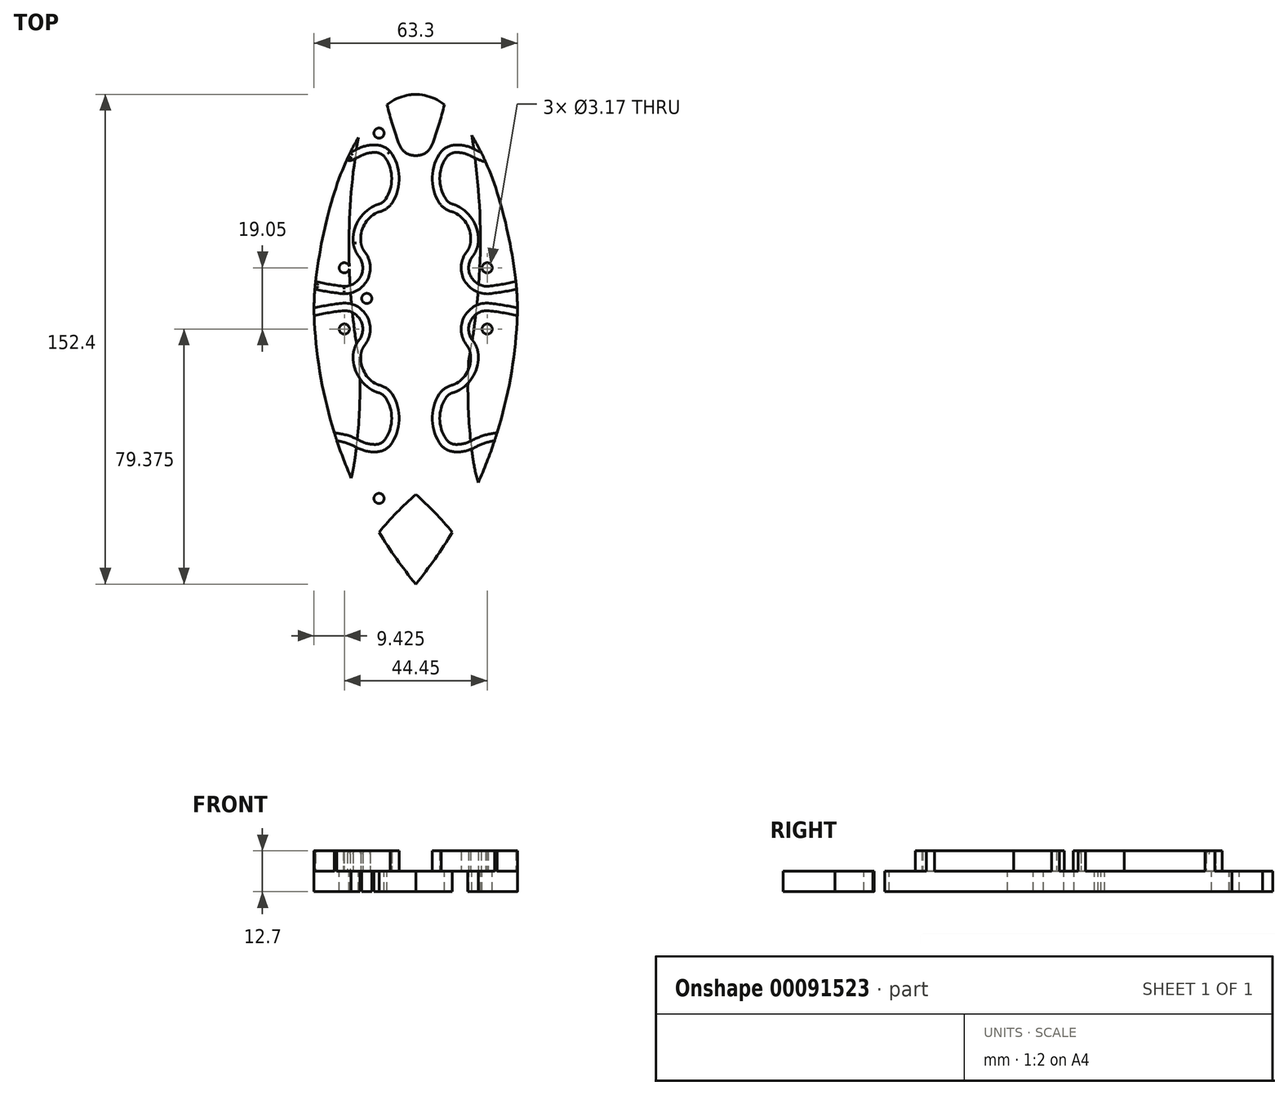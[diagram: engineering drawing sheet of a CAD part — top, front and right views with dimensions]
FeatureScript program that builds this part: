
annotation { "Feature Type Name" : "Feature", "Feature Type Description" : "" }
export const myFeature = defineFeature(function(context is Context, id is Id, definition is map)
    precondition{}
    {
        {
            var Q0;
            Q0=qCreatedBy(makeId("Top.planeOp"),FACE);
            var sketch = newSketch(context, id + "F0", { "sketchPlane" : qUnion([Q0])});
            skLineSegment(sketch, "E0", {"start": v(0, 0) * mm, "end": v(0, 80.69) * mm, "construction": true});
            skLineSegment(sketch, "E1", {"start": v(-64.8, 0) * mm, "end": v(76.72, 0) * mm, "construction": true});
            skLineSegment(sketch, "E2", {"start": v(0, 0) * mm, "end": v(0, -115.81) * mm, "construction": true});
            skPoint(sketch, "E3", {"position": v(0, 63.5) * mm});
            skPoint(sketch, "E4", {"position": v(31.75, 0) * mm});
            skPoint(sketch, "E5", {"position": v(-31.75, 0) * mm});
            skPoint(sketch, "E6", {"position": v(0, -88.9) * mm});
            skPoint(sketch, "E7", {"position": v(0, -19.05) * mm});
            skEllipticalArc(sketch, "E8", {});
            skPoint(sketch, "E9", {"position": v(0, -63.5) * mm});
            skPoint(sketch, "E10", {"position": v(16.51, -63.5) * mm});
            skArc(sketch, "E11", {"start": v(0, -88.9) * mm, "mid": v(22.23, -50.65) * mm, "end": v(31.54, -7.4) * mm});
            skArc(sketch, "E12.MirrorCS", {"start": v(0, -88.9) * mm, "mid": v(-22.23, -50.65) * mm, "end": v(-31.54, -7.4) * mm});
            skArc(sketch, "E13.filletArc", {"start": v(-31.03, 6.47) * mm, "mid": v(-31.6, -0.45) * mm, "end": v(-31.54, -7.4) * mm});
            skArc(sketch, "E14.MirrorCS", {"start": v(31.03, 6.47) * mm, "mid": v(31.6, -0.45) * mm, "end": v(31.54, -7.4) * mm});
            skPoint(sketch, "E15", {"position": v(-19.05, 76.2) * mm});
            skPoint(sketch, "E16", {"position": v(19.05, 76.2) * mm});
            skArc(sketch, "E17", {"start": v(-19.05, 47.97) * mm, "mid": v(-17.86, 62.09) * mm, "end": v(-19.05, 76.2) * mm});
            skArc(sketch, "E18", {"start": v(-19.05, 76.2) * mm, "mid": v(-11.04, 67.58) * mm, "end": v(0, 63.5) * mm});
            skArc(sketch, "E19.MirrorCS", {"start": v(19.05, 47.97) * mm, "mid": v(17.86, 62.09) * mm, "end": v(19.05, 76.2) * mm});
            skArc(sketch, "E20.MirrorCS", {"start": v(19.05, 76.2) * mm, "mid": v(11.04, 67.58) * mm, "end": v(0, 63.5) * mm});
            const initialGuessF0  = {"E8": [0, -0.01905, 0, 1, 0.08255, 0.03263075260586246, 5.026736623577707, 1.2564486836018787]};
            skSetInitialGuess(sketch, initialGuessF0);
            skSolve(sketch);
        }
        {
            var Q0;
            Q0=makeQuery(id+"F0.imprint","IMPRINT",FACE,{"disambiguationData":[TD([[makeQuery(id+"F0.imprint","IMPRINT",EDGE,{"derivedFrom":sQuery(id+"F0.wireOp",EDGE,"E8")}),1.0]])]});
            extrude(context, id + "F1", {"entities" : qUnion([Q0]), "oppositeDirection" : true, "depth" : 6.35 * mm});
        }
        {
            var Q0;
            Q0=qCreatedBy(makeId("Top.planeOp"),FACE);
            var sketch = newSketch(context, id + "F2", { "sketchPlane" : qUnion([Q0])});
            skLineSegment(sketch, "E21", {"start": v(0, -123.95) * mm, "end": v(0, 157.96) * mm, "construction": true});
            skLineSegment(sketch, "E22", {"start": v(104.8, 0) * mm, "end": v(-112.4, 0) * mm, "construction": true});
            skPoint(sketch, "E23", {"position": v(22.23, 0) * mm});
            skPoint(sketch, "E24", {"position": v(22.23, 9.52) * mm});
            skPoint(sketch, "E25", {"position": v(12.7, 0) * mm});
            skPoint(sketch, "E26", {"position": v(12.7, 41.27) * mm});
            skPoint(sketch, "E27", {"position": v(12.7, 33.34) * mm});
            skPoint(sketch, "E28", {"position": v(22.23, -15.88) * mm});
            skPoint(sketch, "E29", {"position": v(19.05, 0) * mm});
            skPoint(sketch, "E30", {"position": v(19.05, -31.46) * mm});
            skPoint(sketch, "E31", {"position": v(19.05, -39.84) * mm});
            skSolve(sketch);
        }
        {
            var Q0;
            Q0=qCreatedBy(makeId("Top.planeOp"),FACE);
            var sketch = newSketch(context, id + "F3", { "sketchPlane" : qUnion([Q0])});
            skPoint(sketch, "E32", {"position": v(76.2, 76.2) * mm});
            skLineSegment(sketch, "E33", {"start": v(-207.32, 0) * mm, "end": v(117.03, 0) * mm, "construction": true});
            skLineSegment(sketch, "E34", {"start": v(0, 0) * mm, "end": v(0, 84.75) * mm, "construction": true});
            skPoint(sketch, "E35", {"position": v(22.22, 9.52) * mm});
            skPoint(sketch, "E36", {"position": v(12.7, 33.34) * mm});
            skPoint(sketch, "E37", {"position": v(12.7, 41.28) * mm});
            skCircle(sketch, "E38", {"center": v(76.2, 76.2) * mm, "radius": 11.11 * mm});
            skArc(sketch, "E39", {"start": v(64.87, 81.94) * mm, "mid": v(76.2, 63.5) * mm, "end": v(87.53, 81.94) * mm});
            skCircle(sketch, "E40", {"center": v(76.2, 76.2) * mm, "radius": 15.88 * mm, "construction": true});
            skArc(sketch, "E41", {"start": v(21.55, 15.04) * mm, "mid": v(16.68, 9.19) * mm, "end": v(22.22, 3.97) * mm});
            skPoint(sketch, "E42", {"position": v(12.7, 27.37) * mm});
            skPoint(sketch, "E43", {"position": v(63.5, 76.2) * mm});
            skPoint(sketch, "E44", {"position": v(88.9, 76.2) * mm});
            skPoint(sketch, "E45", {"position": v(61.91, 63.5) * mm});
            skPoint(sketch, "E46", {"position": v(50.8, 46.04) * mm});
            skPoint(sketch, "E47", {"position": v(31.75, 41.28) * mm});
            skPoint(sketch, "E48", {"position": v(19.05, 42.86) * mm});
            skArc(sketch, "E49", {"start": v(50.8, 46.04) * mm, "mid": v(60.54, 59.7) * mm, "end": v(63.5, 76.2) * mm});
            skArc(sketch, "E50", {"start": v(23.54, 41.87) * mm, "mid": v(37.5, 41.77) * mm, "end": v(50.8, 46.04) * mm});
            skPoint(sketch, "E51", {"position": v(76.2, 127) * mm});
            skLineSegment(sketch, "E52", {"start": v(76.2, 76.2) * mm, "end": v(76.2, 127) * mm, "construction": true});
            skArc(sketch, "E53", {"start": v(77.79, 125.41) * mm, "mid": v(76.2, 127) * mm, "end": v(74.61, 125.41) * mm});
            skPoint(sketch, "E54", {"position": v(77.79, 125.41) * mm});
            skPoint(sketch, "E55", {"position": v(74.61, 125.41) * mm});
            skPoint(sketch, "E56", {"position": v(65.2, 82.55) * mm});
            skLineSegment(sketch, "E57", {"start": v(63.5, 76.2) * mm, "end": v(88.9, 76.2) * mm, "construction": true});
            skPoint(sketch, "E58", {"position": v(87.2, 82.55) * mm});
            skArc(sketch, "E59", {"start": v(77.79, 125.41) * mm, "mid": v(80.38, 104.21) * mm, "end": v(86.68, 83.8) * mm});
            skArc(sketch, "E60", {"start": v(65.72, 83.8) * mm, "mid": v(72.02, 104.21) * mm, "end": v(74.61, 125.41) * mm});
            skArc(sketch, "E61.filletArc", {"start": v(64.87, 81.94) * mm, "mid": v(65.31, 82.86) * mm, "end": v(65.72, 83.8) * mm});
            skArc(sketch, "E62.filletArc", {"start": v(86.68, 83.8) * mm, "mid": v(87.09, 82.86) * mm, "end": v(87.53, 81.94) * mm});
            skArc(sketch, "E63", {"start": v(87.53, 81.94) * mm, "mid": v(76.2, 88.9) * mm, "end": v(64.87, 81.94) * mm});
            skArc(sketch, "E64.0", {"start": v(80.56, 91.46) * mm, "mid": v(76.36, 92.07) * mm, "end": v(72.16, 91.55) * mm});
            skArc(sketch, "E65", {"start": v(76.52, 107.95) * mm, "mid": v(76.2, 108.27) * mm, "end": v(75.88, 107.95) * mm});
            skPoint(sketch, "E66", {"position": v(75.88, 107.95) * mm});
            skPoint(sketch, "E67", {"position": v(76.52, 107.95) * mm});
            skArc(sketch, "E68", {"start": v(72.16, 91.55) * mm, "mid": v(74.3, 99.69) * mm, "end": v(75.88, 107.95) * mm});
            skArc(sketch, "E69", {"start": v(76.52, 107.95) * mm, "mid": v(78.26, 99.64) * mm, "end": v(80.56, 91.46) * mm});
            skPoint(sketch, "E70", {"position": v(22.22, 3.97) * mm});
            skPoint(sketch, "E71", {"position": v(16.67, 9.52) * mm});
            skPoint(sketch, "E72", {"position": v(22.22, 15.08) * mm});
            skPoint(sketch, "E73", {"position": v(57.54, 53.98) * mm});
            skCircle(sketch, "E74", {"center": v(67.48, 46.06) * mm, "radius": 12.7 * mm, "construction": true});
            skLineSegment(sketch, "E75.bottom", {"start": v(57.54, 53.98) * mm, "end": v(77.4, 53.98) * mm, "construction": true});
            skLineSegment(sketch, "E75.top", {"start": v(57.54, 38.15) * mm, "end": v(77.4, 38.15) * mm, "construction": true});
            skLineSegment(sketch, "E75.left", {"start": v(57.54, 53.98) * mm, "end": v(57.54, 38.15) * mm, "construction": true});
            skLineSegment(sketch, "E75.right", {"start": v(77.4, 53.97) * mm, "end": v(77.4, 38.15) * mm, "construction": true});
            skArc(sketch, "E76", {"start": v(22.22, 3.97) * mm, "mid": v(69.22, 27.48) * mm, "end": v(88.9, 76.2) * mm});
            skCircle(sketch, "E77", {"center": v(12.7, 33.34) * mm, "radius": 3.97 * mm, "construction": true});
            skPoint(sketch, "E78", {"position": v(12.7, 45.24) * mm});
            skPoint(sketch, "E79", {"position": v(8.73, 41.28) * mm});
            skLineSegment(sketch, "E80.bottom", {"start": v(8.73, 41.28) * mm, "end": v(12.7, 41.28) * mm, "construction": true});
            skLineSegment(sketch, "E80.top", {"start": v(8.73, 45.24) * mm, "end": v(12.7, 45.24) * mm, "construction": true});
            skLineSegment(sketch, "E80.left", {"start": v(8.73, 41.28) * mm, "end": v(8.73, 45.24) * mm, "construction": true});
            skLineSegment(sketch, "E80.right", {"start": v(12.7, 41.28) * mm, "end": v(12.7, 45.24) * mm, "construction": true});
            skLineSegment(sketch, "E81", {"start": v(12.7, 41.27) * mm, "end": v(8.73, 45.24) * mm, "construction": true});
            skPoint(sketch, "E82", {"position": v(9.9, 44.08) * mm});
            skPoint(sketch, "E83", {"position": v(12.7, 37.3) * mm});
            skLineSegment(sketch, "E84", {"start": v(12.7, 37.3) * mm, "end": v(0, 37.3) * mm, "construction": true});
            skPoint(sketch, "E85.MirrorP", {"position": v(9.9, 30.53) * mm});
            skArc(sketch, "E86", {"start": v(9.9, 44.08) * mm, "mid": v(7.67, 37.3) * mm, "end": v(9.9, 30.53) * mm});
            skArc(sketch, "E87", {"start": v(12.7, 45.24) * mm, "mid": v(11.18, 44.94) * mm, "end": v(9.9, 44.08) * mm});
            skArc(sketch, "E88.MirrorCS", {"start": v(12.09, 29.42) * mm, "mid": v(10.9, 29.8) * mm, "end": v(9.9, 30.53) * mm});
            skArc(sketch, "E89", {"start": v(17.4, 44.02) * mm, "mid": v(15.13, 44.93) * mm, "end": v(12.7, 45.24) * mm});
            skArc(sketch, "E90.filletArc", {"start": v(17.4, 44.02) * mm, "mid": v(20.38, 42.68) * mm, "end": v(23.54, 41.87) * mm});
            skLineSegment(sketch, "E91", {"start": v(12.7, 37.3) * mm, "end": v(22.22, 9.52) * mm, "construction": true});
            skPoint(sketch, "E92", {"position": v(17.46, 23.42) * mm});
            skArc(sketch, "E93", {"start": v(17.46, 23.42) * mm, "mid": v(59, 36.27) * mm, "end": v(76.2, 76.2) * mm, "construction": true});
            skPoint(sketch, "E94", {"position": v(46.35, 27.89) * mm});
            skArc(sketch, "E95", {"start": v(23.97, 15.5) * mm, "mid": v(35.96, 20.26) * mm, "end": v(46.35, 27.89) * mm});
            skArc(sketch, "E96", {"start": v(13.98, 29.02) * mm, "mid": v(30.1, 26.65) * mm, "end": v(46.35, 27.89) * mm});
            skPoint(sketch, "E97.visualSharp", {"position": v(12.7, 29.37) * mm});
            skArc(sketch, "E97.filletArc", {"start": v(13.98, 29.02) * mm, "mid": v(13.04, 29.24) * mm, "end": v(12.09, 29.42) * mm});
            skArc(sketch, "E98.filletArc", {"start": v(21.55, 15.04) * mm, "mid": v(22.77, 15.23) * mm, "end": v(23.97, 15.5) * mm});
            skPoint(sketch, "E99", {"position": v(76.2, 92.08) * mm});
            skArc(sketch, "E100.MirrorCS", {"start": v(22.22, -3.97) * mm, "mid": v(69.22, -27.48) * mm, "end": v(88.9, -76.2) * mm});
            skArc(sketch, "E101.MirrorCS", {"start": v(21.55, -15.04) * mm, "mid": v(16.68, -9.19) * mm, "end": v(22.22, -3.97) * mm});
            skArc(sketch, "E102.MirrorCS", {"start": v(23.97, -15.5) * mm, "mid": v(35.96, -20.26) * mm, "end": v(46.35, -27.89) * mm});
            skArc(sketch, "E103.MirrorCS", {"start": v(13.98, -29.02) * mm, "mid": v(30.1, -26.65) * mm, "end": v(46.35, -27.89) * mm});
            skCircle(sketch, "E104.MirrorC", {"center": v(76.2, -76.2) * mm, "radius": 11.11 * mm});
            skArc(sketch, "E105.MirrorCS", {"start": v(64.87, -81.94) * mm, "mid": v(76.2, -63.5) * mm, "end": v(87.53, -81.94) * mm});
            skArc(sketch, "E106.MirrorCS", {"start": v(23.54, -41.87) * mm, "mid": v(37.5, -41.77) * mm, "end": v(50.8, -46.04) * mm});
            skArc(sketch, "E107.MirrorCS", {"start": v(77.79, -125.41) * mm, "mid": v(80.38, -104.21) * mm, "end": v(86.68, -83.8) * mm});
            skArc(sketch, "E108.MirrorCS", {"start": v(76.52, -107.95) * mm, "mid": v(78.26, -99.64) * mm, "end": v(80.56, -91.46) * mm});
            skArc(sketch, "E109.MirrorCS", {"start": v(72.16, -91.55) * mm, "mid": v(74.3, -99.69) * mm, "end": v(75.88, -107.95) * mm});
            skArc(sketch, "E110.MirrorCS", {"start": v(65.72, -83.8) * mm, "mid": v(72.02, -104.21) * mm, "end": v(74.61, -125.41) * mm});
            skArc(sketch, "E111.MirrorCS", {"start": v(80.56, -91.46) * mm, "mid": v(76.36, -92.07) * mm, "end": v(72.16, -91.55) * mm});
            skCircle(sketch, "E112.MirrorC", {"center": v(67.48, -46.06) * mm, "radius": 12.7 * mm, "construction": true});
            skArc(sketch, "E113.MirrorCS", {"start": v(50.8, -46.04) * mm, "mid": v(60.54, -59.7) * mm, "end": v(63.5, -76.2) * mm});
            skCircle(sketch, "E114.MirrorC", {"center": v(12.7, -33.34) * mm, "radius": 3.97 * mm, "construction": true});
            skCircle(sketch, "E115.MirrorC", {"center": v(12.7, -41.28) * mm, "radius": 3.97 * mm, "construction": true});
            skArc(sketch, "E116.MirrorCS", {"start": v(9.9, -44.08) * mm, "mid": v(7.67, -37.3) * mm, "end": v(9.9, -30.53) * mm});
            skArc(sketch, "E117.MirrorCS", {"start": v(13.98, -29.02) * mm, "mid": v(13.04, -29.24) * mm, "end": v(12.09, -29.42) * mm});
            skArc(sketch, "E118.MirrorCS", {"start": v(12.09, -29.42) * mm, "mid": v(10.9, -29.8) * mm, "end": v(9.9, -30.53) * mm});
            skArc(sketch, "E119.MirrorCS", {"start": v(17.4, -44.02) * mm, "mid": v(20.38, -42.68) * mm, "end": v(23.54, -41.87) * mm});
            skArc(sketch, "E120.MirrorCS", {"start": v(17.4, -44.02) * mm, "mid": v(15.13, -44.93) * mm, "end": v(12.7, -45.24) * mm});
            skArc(sketch, "E121.MirrorCS", {"start": v(21.55, -15.04) * mm, "mid": v(22.77, -15.23) * mm, "end": v(23.97, -15.5) * mm});
            skArc(sketch, "E122.0", {"start": v(13.33, 26.56) * mm, "mid": v(30.01, 24.11) * mm, "end": v(46.83, 25.4) * mm});
            skArc(sketch, "E122.1", {"start": v(13.33, 26.56) * mm, "mid": v(12.52, 26.76) * mm, "end": v(11.7, 26.9) * mm});
            skArc(sketch, "E122.2", {"start": v(18.64, 46.24) * mm, "mid": v(15.77, 47.4) * mm, "end": v(12.7, 47.78) * mm});
            skArc(sketch, "E122.3", {"start": v(12.7, 47.78) * mm, "mid": v(10.11, 47.25) * mm, "end": v(7.95, 45.73) * mm});
            skArc(sketch, "E122.4", {"start": v(7.95, 45.73) * mm, "mid": v(5.13, 37.3) * mm, "end": v(7.95, 28.88) * mm});
            skArc(sketch, "E122.5", {"start": v(11.7, 26.9) * mm, "mid": v(9.66, 27.58) * mm, "end": v(7.95, 28.88) * mm});
            skArc(sketch, "E123.0", {"start": v(18.64, 46.24) * mm, "mid": v(21.22, 45.08) * mm, "end": v(23.96, 44.37) * mm});
            skSolve(sketch);
        }
        {
            var Q0;
            Q0 = qSketchRegion(id + "F3", true);
            var sketch = newSketch(context, id + "F4", { "sketchPlane" : qUnion([Q0])});
            skFitSpline(sketch, "E124.0", {"points": [v(0, 63.5) * mm, v(-8.65, 63.5) * mm, v(-16.95, 54.8) * mm, v(-29.2, 23.84) * mm, v(-32.63, 2.84) * mm, v(-32.63, -40.94) * mm, v(-29.2, -61.94) * mm, v(-16.95, -92.9) * mm, v(-8.65, -101.6) * mm, v(8.65, -101.6) * mm, v(16.95, -92.9) * mm, v(29.2, -61.94) * mm, v(32.63, -40.94) * mm, v(32.63, 2.84) * mm, v(29.2, 23.84) * mm, v(16.95, 54.8) * mm, v(8.65, 63.5) * mm, v(0, 63.5) * mm]});
            skArc(sketch, "E125.0", {"start": v(23.34, 17.96) * mm, "mid": v(26.1, 18.75) * mm, "end": v(28.8, 19.71) * mm});
            skArc(sketch, "E125.1", {"start": v(21.24, 17.56) * mm, "mid": v(22.3, 17.73) * mm, "end": v(23.34, 17.96) * mm});
            skArc(sketch, "E125.2", {"start": v(21.24, 17.56) * mm, "mid": v(14.15, 8.96) * mm, "end": v(22.37, 1.43) * mm});
            skArc(sketch, "E125.3", {"start": v(22.37, 1.43) * mm, "mid": v(26.9, 2.03) * mm, "end": v(31.4, 2.9) * mm});
            skArc(sketch, "E126.0", {"start": v(22.23, 3.78) * mm, "mid": v(26.73, 4.38) * mm, "end": v(31.18, 5.25) * mm});
            skArc(sketch, "E126.1", {"start": v(21.53, 15.23) * mm, "mid": v(16.49, 9.17) * mm, "end": v(22.23, 3.78) * mm});
            skArc(sketch, "E126.2", {"start": v(21.53, 15.23) * mm, "mid": v(22.73, 15.42) * mm, "end": v(23.93, 15.68) * mm});
            skArc(sketch, "E126.3", {"start": v(23.93, 15.68) * mm, "mid": v(26.63, 16.45) * mm, "end": v(29.28, 17.38) * mm});
            skFitSpline(sketch, "E127.0", {"points": [v(0, 63.5) * mm, v(-8.65, 63.5) * mm, v(-16.95, 54.8) * mm, v(-29.2, 23.84) * mm, v(-32.63, 2.84) * mm, v(-32.63, -40.94) * mm, v(-29.2, -61.94) * mm, v(-16.95, -92.9) * mm, v(-8.65, -101.6) * mm, v(8.65, -101.6) * mm, v(16.95, -92.9) * mm, v(29.2, -61.94) * mm, v(32.63, -40.94) * mm, v(32.63, 2.84) * mm, v(29.2, 23.84) * mm, v(16.95, 54.8) * mm, v(8.65, 63.5) * mm, v(0, 63.5) * mm]});
            skFitSpline(sketch, "E128.0", {"points": [v(0, 63.5) * mm, v(-8.65, 63.5) * mm, v(-16.95, 54.8) * mm, v(-29.2, 23.84) * mm, v(-32.63, 2.84) * mm, v(-32.63, -40.94) * mm, v(-29.2, -61.94) * mm, v(-16.95, -92.9) * mm, v(-8.65, -101.6) * mm, v(8.65, -101.6) * mm, v(16.95, -92.9) * mm, v(29.2, -61.94) * mm, v(32.63, -40.94) * mm, v(32.63, 2.84) * mm, v(29.2, 23.84) * mm, v(16.95, 54.8) * mm, v(8.65, 63.5) * mm, v(0, 63.5) * mm]});
            skLineSegment(sketch, "E129", {"start": v(27.18, 26.62) * mm, "end": v(27.79, 24.22) * mm});
            skArc(sketch, "E130.MirrorCS", {"start": v(-21.24, 17.56) * mm, "mid": v(-14.15, 8.96) * mm, "end": v(-22.37, 1.43) * mm});
            skArc(sketch, "E131.MirrorCS", {"start": v(-21.24, 17.56) * mm, "mid": v(-22.3, 17.73) * mm, "end": v(-23.34, 17.96) * mm});
            skArc(sketch, "E132.MirrorCS", {"start": v(-23.34, 17.96) * mm, "mid": v(-26.1, 18.75) * mm, "end": v(-28.8, 19.71) * mm});
            skArc(sketch, "E133.MirrorCS", {"start": v(-23.93, 15.68) * mm, "mid": v(-26.63, 16.45) * mm, "end": v(-29.28, 17.38) * mm});
            skArc(sketch, "E134.MirrorCS", {"start": v(-21.53, 15.23) * mm, "mid": v(-22.73, 15.42) * mm, "end": v(-23.93, 15.68) * mm});
            skArc(sketch, "E135.MirrorCS", {"start": v(-21.53, 15.23) * mm, "mid": v(-16.49, 9.17) * mm, "end": v(-22.23, 3.78) * mm});
            skArc(sketch, "E136.MirrorCS", {"start": v(-22.23, 3.78) * mm, "mid": v(-26.73, 4.38) * mm, "end": v(-31.18, 5.25) * mm});
            skArc(sketch, "E137.MirrorCS", {"start": v(-22.37, 1.43) * mm, "mid": v(-26.9, 2.03) * mm, "end": v(-31.4, 2.9) * mm});
            skArc(sketch, "E138.MirrorCS", {"start": v(-31.18, 5.25) * mm, "mid": v(-31.3, 4.07) * mm, "end": v(-31.4, 2.9) * mm});
            skArc(sketch, "E139.MirrorCS", {"start": v(21.24, -17.56) * mm, "mid": v(14.15, -8.96) * mm, "end": v(22.37, -1.43) * mm});
            skArc(sketch, "E140.MirrorCS", {"start": v(21.53, -15.23) * mm, "mid": v(16.49, -9.17) * mm, "end": v(22.23, -3.78) * mm});
            skArc(sketch, "E141.MirrorCS", {"start": v(21.24, -17.56) * mm, "mid": v(22.3, -17.73) * mm, "end": v(23.34, -17.96) * mm});
            skArc(sketch, "E142.MirrorCS", {"start": v(21.53, -15.23) * mm, "mid": v(22.73, -15.42) * mm, "end": v(23.93, -15.68) * mm});
            skPoint(sketch, "E143.MirrorCS.end.orphan", {"position": v(-28.8, -19.71) * mm});
            skPoint(sketch, "E143.MirrorCS.start.orphan", {"position": v(-23.34, -17.96) * mm});
            skPoint(sketch, "E144.MirrorCS.end.orphan", {"position": v(-29.28, -17.38) * mm});
            skPoint(sketch, "E144.MirrorCS.start.orphan", {"position": v(-23.93, -15.68) * mm});
            skPoint(sketch, "E145.MirrorCS.end.orphan", {"position": v(-31.18, -5.25) * mm});
            skPoint(sketch, "E145.MirrorCS.start.orphan", {"position": v(-22.23, -3.78) * mm});
            skPoint(sketch, "E146.MirrorCS.end.orphan", {"position": v(-31.4, -2.9) * mm});
            skPoint(sketch, "E146.MirrorCS.start.orphan", {"position": v(-22.37, -1.43) * mm});
            skPoint(sketch, "E147.MirrorCS.end.orphan", {"position": v(31.4, -2.9) * mm});
            skPoint(sketch, "E147.MirrorCS.start.orphan", {"position": v(31.18, -5.25) * mm});
            skArc(sketch, "E148.0", {"start": v(31.18, 5.25) * mm, "mid": v(31.3, 4.07) * mm, "end": v(31.4, 2.9) * mm});
            skArc(sketch, "E148.1", {"start": v(30.24, -20.3) * mm, "mid": v(30.41, -19.1) * mm, "end": v(30.57, -17.89) * mm});
            skPoint(sketch, "E149.MirrorCS.start.orphan", {"position": v(22.23, -3.78) * mm});
            skPoint(sketch, "E150.MirrorCS.start.orphan", {"position": v(22.37, -1.43) * mm});
            skPoint(sketch, "E151.MirrorCS.end.orphan", {"position": v(29.28, -17.38) * mm});
            skPoint(sketch, "E151.MirrorCS.start.orphan", {"position": v(23.93, -15.68) * mm});
            skPoint(sketch, "E152.MirrorCS.end.orphan", {"position": v(28.8, -19.71) * mm});
            skPoint(sketch, "E152.MirrorCS.start.orphan", {"position": v(23.34, -17.96) * mm});
            skArc(sketch, "E153.0", {"start": v(22.48, -1.44) * mm, "mid": v(27.1, -2.06) * mm, "end": v(31.65, -2.95) * mm});
            skArc(sketch, "E154.0", {"start": v(22.24, -3.78) * mm, "mid": v(26.96, -4.42) * mm, "end": v(31.62, -5.35) * mm});
            skArc(sketch, "E155.0", {"start": v(23.34, -17.96) * mm, "mid": v(26.83, -19) * mm, "end": v(30.24, -20.3) * mm});
            skArc(sketch, "E156.0", {"start": v(23.93, -15.68) * mm, "mid": v(27.29, -16.67) * mm, "end": v(30.57, -17.89) * mm});
            skArc(sketch, "E157.trimOffspring", {"start": v(31.65, -2.95) * mm, "mid": v(31.65, -4.15) * mm, "end": v(31.62, -5.35) * mm});
            skArc(sketch, "E158", {"start": v(22.48, -1.44) * mm, "mid": v(22.43, -1.43) * mm, "end": v(22.37, -1.43) * mm});
            skArc(sketch, "E159", {"start": v(22.24, -3.78) * mm, "mid": v(22.24, -3.78) * mm, "end": v(22.23, -3.78) * mm});
            skArc(sketch, "E160", {"start": v(-28.8, 19.71) * mm, "mid": v(-29.07, 18.55) * mm, "end": v(-29.28, 17.38) * mm});
            skArc(sketch, "E161.MirrorCS", {"start": v(-31.65, -2.95) * mm, "mid": v(-31.65, -4.15) * mm, "end": v(-31.62, -5.35) * mm});
            skArc(sketch, "E162.MirrorCS", {"start": v(-22.48, -1.44) * mm, "mid": v(-27.1, -2.06) * mm, "end": v(-31.65, -2.95) * mm});
            skArc(sketch, "E163.MirrorCS", {"start": v(-22.24, -3.78) * mm, "mid": v(-26.96, -4.42) * mm, "end": v(-31.62, -5.35) * mm});
            skArc(sketch, "E164.MirrorCS", {"start": v(-21.53, -15.23) * mm, "mid": v(-16.49, -9.17) * mm, "end": v(-22.23, -3.78) * mm});
            skArc(sketch, "E165.MirrorCS", {"start": v(-21.24, -17.56) * mm, "mid": v(-14.15, -8.96) * mm, "end": v(-22.37, -1.43) * mm});
            skArc(sketch, "E166.MirrorCS", {"start": v(-22.48, -1.44) * mm, "mid": v(-22.43, -1.43) * mm, "end": v(-22.37, -1.43) * mm});
            skArc(sketch, "E167.MirrorCS", {"start": v(-22.24, -3.78) * mm, "mid": v(-22.24, -3.78) * mm, "end": v(-22.23, -3.78) * mm});
            skArc(sketch, "E168.MirrorCS", {"start": v(-21.53, -15.23) * mm, "mid": v(-22.73, -15.42) * mm, "end": v(-23.93, -15.68) * mm});
            skArc(sketch, "E169.MirrorCS", {"start": v(-21.24, -17.56) * mm, "mid": v(-22.3, -17.73) * mm, "end": v(-23.34, -17.96) * mm});
            skArc(sketch, "E170.MirrorCS", {"start": v(-23.34, -17.96) * mm, "mid": v(-26.83, -19) * mm, "end": v(-30.24, -20.3) * mm});
            skArc(sketch, "E171.MirrorCS", {"start": v(-23.93, -15.68) * mm, "mid": v(-27.29, -16.67) * mm, "end": v(-30.57, -17.89) * mm});
            skArc(sketch, "E172.MirrorCS", {"start": v(-30.24, -20.3) * mm, "mid": v(-30.41, -19.1) * mm, "end": v(-30.57, -17.89) * mm});
            skLineSegment(sketch, "E173", {"start": v(-51.74, 0) * mm, "end": v(55.96, 0) * mm, "construction": true});
            skLineSegment(sketch, "E174", {"start": v(0, 72.52) * mm, "end": v(0, -77) * mm, "construction": true});
            skSolve(sketch);
        }
        {
            var Q0;
            Q0=qCreatedBy(makeId("Top.planeOp"),FACE);
            var sketch = newSketch(context, id + "F5", { "sketchPlane" : qUnion([Q0])});
            skArc(sketch, "E175", {"start": v(21.77, 42.45) * mm, "mid": v(21.1, 43.93) * mm, "end": v(20.4, 45.4) * mm});
            skArc(sketch, "E176", {"start": v(27.79, 24.22) * mm, "mid": v(27.51, 25.43) * mm, "end": v(27.18, 26.62) * mm});
            skArc(sketch, "E177.0", {"start": v(17.5, 44.19) * mm, "mid": v(19.58, 43.19) * mm, "end": v(21.77, 42.45) * mm});
            skArc(sketch, "E177.1", {"start": v(13.93, 28.84) * mm, "mid": v(20.5, 27.43) * mm, "end": v(27.18, 26.62) * mm});
            skArc(sketch, "E177.2", {"start": v(13.93, 28.84) * mm, "mid": v(12.97, 29.06) * mm, "end": v(12, 29.24) * mm});
            skArc(sketch, "E177.3", {"start": v(9.42, 43.73) * mm, "mid": v(7.48, 37.32) * mm, "end": v(9.4, 30.9) * mm});
            skArc(sketch, "E177.4", {"start": v(17.5, 44.19) * mm, "mid": v(15.1, 45.14) * mm, "end": v(12.52, 45.43) * mm});
            skPoint(sketch, "E178.visualSharp", {"position": v(10.58, 29.4) * mm});
            skArc(sketch, "E178.filletArc", {"start": v(9.4, 30.9) * mm, "mid": v(10.53, 29.8) * mm, "end": v(12, 29.24) * mm});
            skPoint(sketch, "E179.visualSharp", {"position": v(10.57, 45.2) * mm});
            skArc(sketch, "E179.filletArc", {"start": v(12.52, 45.43) * mm, "mid": v(10.76, 44.96) * mm, "end": v(9.42, 43.73) * mm});
            skArc(sketch, "E180.0", {"start": v(18.64, 46.24) * mm, "mid": v(19.5, 45.8) * mm, "end": v(20.4, 45.4) * mm});
            skArc(sketch, "E180.1", {"start": v(18.64, 46.24) * mm, "mid": v(15.77, 47.4) * mm, "end": v(12.7, 47.78) * mm});
            skArc(sketch, "E180.2", {"start": v(12.7, 47.78) * mm, "mid": v(10.11, 47.25) * mm, "end": v(7.95, 45.73) * mm});
            skArc(sketch, "E180.3", {"start": v(13.33, 26.56) * mm, "mid": v(20.5, 25.05) * mm, "end": v(27.79, 24.22) * mm});
            skArc(sketch, "E180.4", {"start": v(13.33, 26.56) * mm, "mid": v(12.52, 26.76) * mm, "end": v(11.7, 26.9) * mm});
            skArc(sketch, "E180.5", {"start": v(11.7, 26.9) * mm, "mid": v(9.66, 27.58) * mm, "end": v(7.95, 28.88) * mm});
            skArc(sketch, "E180.6", {"start": v(7.95, 45.73) * mm, "mid": v(5.13, 37.3) * mm, "end": v(7.95, 28.88) * mm});
            skArc(sketch, "E181.MirrorCS", {"start": v(-7.95, 45.73) * mm, "mid": v(-5.13, 37.3) * mm, "end": v(-7.95, 28.88) * mm});
            skArc(sketch, "E182.MirrorCS", {"start": v(-12.7, 47.78) * mm, "mid": v(-10.11, 47.25) * mm, "end": v(-7.95, 45.73) * mm});
            skArc(sketch, "E183.MirrorCS", {"start": v(-18.64, 46.24) * mm, "mid": v(-15.77, 47.4) * mm, "end": v(-12.7, 47.78) * mm});
            skArc(sketch, "E184.MirrorCS", {"start": v(-12.52, 45.43) * mm, "mid": v(-10.76, 44.96) * mm, "end": v(-9.42, 43.73) * mm});
            skArc(sketch, "E185.MirrorCS", {"start": v(-9.42, 43.73) * mm, "mid": v(-7.48, 37.32) * mm, "end": v(-9.4, 30.9) * mm});
            skArc(sketch, "E186.MirrorCS", {"start": v(-9.4, 30.9) * mm, "mid": v(-10.53, 29.8) * mm, "end": v(-12, 29.24) * mm});
            skArc(sketch, "E187.MirrorCS", {"start": v(-11.7, 26.9) * mm, "mid": v(-9.66, 27.58) * mm, "end": v(-7.95, 28.88) * mm});
            skArc(sketch, "E188.MirrorCS", {"start": v(-13.33, 26.56) * mm, "mid": v(-12.52, 26.76) * mm, "end": v(-11.7, 26.9) * mm});
            skArc(sketch, "E189.MirrorCS", {"start": v(-13.93, 28.84) * mm, "mid": v(-12.97, 29.06) * mm, "end": v(-12, 29.24) * mm});
            skArc(sketch, "E190.MirrorCS", {"start": v(-13.93, 28.84) * mm, "mid": v(-20.5, 27.43) * mm, "end": v(-27.18, 26.62) * mm});
            skArc(sketch, "E191.MirrorCS", {"start": v(-13.33, 26.56) * mm, "mid": v(-20.5, 25.05) * mm, "end": v(-27.79, 24.22) * mm});
            skArc(sketch, "E192.MirrorCS", {"start": v(-17.5, 44.19) * mm, "mid": v(-19.58, 43.19) * mm, "end": v(-21.77, 42.45) * mm});
            skArc(sketch, "E193.MirrorCS", {"start": v(-17.5, 44.19) * mm, "mid": v(-15.1, 45.14) * mm, "end": v(-12.52, 45.43) * mm});
            skArc(sketch, "E194.MirrorCS", {"start": v(-18.64, 46.24) * mm, "mid": v(-19.5, 45.8) * mm, "end": v(-20.4, 45.4) * mm});
            skArc(sketch, "E195.MirrorCS", {"start": v(-21.77, 42.45) * mm, "mid": v(-21.1, 43.93) * mm, "end": v(-20.4, 45.4) * mm});
            skArc(sketch, "E196.MirrorCS", {"start": v(-27.79, 24.22) * mm, "mid": v(-27.51, 25.43) * mm, "end": v(-27.18, 26.62) * mm});
            skArc(sketch, "E197.MirrorCS", {"start": v(13.33, -26.56) * mm, "mid": v(12.52, -26.76) * mm, "end": v(11.7, -26.9) * mm});
            skArc(sketch, "E198.MirrorCS", {"start": v(11.7, -26.9) * mm, "mid": v(9.66, -27.58) * mm, "end": v(7.95, -28.88) * mm});
            skArc(sketch, "E199.MirrorCS", {"start": v(7.95, -45.73) * mm, "mid": v(5.13, -37.3) * mm, "end": v(7.95, -28.88) * mm});
            skArc(sketch, "E200.MirrorCS", {"start": v(12.7, -47.78) * mm, "mid": v(10.11, -47.25) * mm, "end": v(7.95, -45.73) * mm});
            skArc(sketch, "E201.MirrorCS", {"start": v(9.42, -43.73) * mm, "mid": v(7.48, -37.32) * mm, "end": v(9.4, -30.9) * mm});
            skArc(sketch, "E202.MirrorCS", {"start": v(9.4, -30.9) * mm, "mid": v(10.53, -29.8) * mm, "end": v(12, -29.24) * mm});
            skArc(sketch, "E203.MirrorCS", {"start": v(13.93, -28.84) * mm, "mid": v(12.97, -29.06) * mm, "end": v(12, -29.24) * mm});
            skArc(sketch, "E204.MirrorCS", {"start": v(17.5, -44.19) * mm, "mid": v(15.1, -45.14) * mm, "end": v(12.52, -45.43) * mm});
            skArc(sketch, "E205.MirrorCS", {"start": v(12.52, -45.43) * mm, "mid": v(10.76, -44.96) * mm, "end": v(9.42, -43.73) * mm});
            skArc(sketch, "E206.MirrorCS", {"start": v(18.64, -46.24) * mm, "mid": v(15.77, -47.4) * mm, "end": v(12.7, -47.78) * mm});
            skArc(sketch, "E207.0", {"start": v(24.52, -44.28) * mm, "mid": v(24.93, -43.04) * mm, "end": v(25.32, -41.8) * mm});
            skPoint(sketch, "E208.MirrorCS.end.orphan", {"position": v(27.18, -26.62) * mm});
            skPoint(sketch, "E208.MirrorCS.start.orphan", {"position": v(13.93, -28.84) * mm});
            skPoint(sketch, "E209.MirrorCS.end.orphan", {"position": v(27.79, -24.22) * mm});
            skPoint(sketch, "E209.MirrorCS.start.orphan", {"position": v(13.33, -26.56) * mm});
            skPoint(sketch, "E210.MirrorCS.end.orphan", {"position": v(21.77, -42.45) * mm});
            skPoint(sketch, "E210.MirrorCS.start.orphan", {"position": v(17.5, -44.19) * mm});
            skPoint(sketch, "E211.MirrorCS.end.orphan", {"position": v(20.4, -45.4) * mm});
            skPoint(sketch, "E211.MirrorCS.start.orphan", {"position": v(18.64, -46.24) * mm});
            skArc(sketch, "E212.0", {"start": v(13.33, -26.56) * mm, "mid": v(21.4, -24.9) * mm, "end": v(29.62, -24.13) * mm});
            skArc(sketch, "E213.0", {"start": v(13.93, -28.84) * mm, "mid": v(21.5, -27.27) * mm, "end": v(29.18, -26.5) * mm});
            skArc(sketch, "E214.0", {"start": v(23.96, -44.37) * mm, "mid": v(24.24, -44.33) * mm, "end": v(24.52, -44.28) * mm});
            skArc(sketch, "E214.1", {"start": v(18.64, -46.24) * mm, "mid": v(21.22, -45.08) * mm, "end": v(23.96, -44.37) * mm});
            skArc(sketch, "E215.0", {"start": v(23.57, -42.06) * mm, "mid": v(24.45, -41.92) * mm, "end": v(25.32, -41.8) * mm});
            skArc(sketch, "E215.1", {"start": v(17.5, -44.19) * mm, "mid": v(20.44, -42.86) * mm, "end": v(23.57, -42.06) * mm});
            skArc(sketch, "E216.trimOffspring", {"start": v(29.18, -26.5) * mm, "mid": v(29.4, -25.31) * mm, "end": v(29.62, -24.13) * mm});
            skArc(sketch, "E217.MirrorCS", {"start": v(-23.57, -42.06) * mm, "mid": v(-24.45, -41.92) * mm, "end": v(-25.32, -41.8) * mm});
            skArc(sketch, "E218.MirrorCS", {"start": v(-23.96, -44.37) * mm, "mid": v(-24.24, -44.33) * mm, "end": v(-24.52, -44.28) * mm});
            skArc(sketch, "E219.MirrorCS", {"start": v(-13.33, -26.56) * mm, "mid": v(-12.52, -26.76) * mm, "end": v(-11.7, -26.9) * mm});
            skPoint(sketch, "E220.MirrorP", {"position": v(-21.77, -42.45) * mm});
            skArc(sketch, "E221.MirrorCS", {"start": v(-13.93, -28.84) * mm, "mid": v(-12.97, -29.06) * mm, "end": v(-12, -29.24) * mm});
            skArc(sketch, "E222.MirrorCS", {"start": v(-17.5, -44.19) * mm, "mid": v(-20.44, -42.86) * mm, "end": v(-23.57, -42.06) * mm});
            skArc(sketch, "E223.MirrorCS", {"start": v(-18.64, -46.24) * mm, "mid": v(-15.77, -47.4) * mm, "end": v(-12.7, -47.78) * mm});
            skArc(sketch, "E224.MirrorCS", {"start": v(-11.7, -26.9) * mm, "mid": v(-9.66, -27.58) * mm, "end": v(-7.95, -28.88) * mm});
            skPoint(sketch, "E225.MirrorP", {"position": v(-17.5, -44.19) * mm});
            skArc(sketch, "E226.MirrorCS", {"start": v(-18.64, -46.24) * mm, "mid": v(-21.22, -45.08) * mm, "end": v(-23.96, -44.37) * mm});
            skPoint(sketch, "E227.MirrorP", {"position": v(-20.4, -45.4) * mm});
            skArc(sketch, "E228.MirrorCS", {"start": v(-7.95, -45.73) * mm, "mid": v(-5.13, -37.3) * mm, "end": v(-7.95, -28.88) * mm});
            skPoint(sketch, "E229.MirrorP", {"position": v(-27.79, -24.22) * mm});
            skArc(sketch, "E230.MirrorCS", {"start": v(-12.52, -45.43) * mm, "mid": v(-10.76, -44.96) * mm, "end": v(-9.42, -43.73) * mm});
            skArc(sketch, "E231.MirrorCS", {"start": v(-17.5, -44.19) * mm, "mid": v(-15.1, -45.14) * mm, "end": v(-12.52, -45.43) * mm});
            skPoint(sketch, "E232.MirrorP", {"position": v(-18.64, -46.24) * mm});
            skArc(sketch, "E233.MirrorCS", {"start": v(-9.4, -30.9) * mm, "mid": v(-10.53, -29.8) * mm, "end": v(-12, -29.24) * mm});
            skArc(sketch, "E234.MirrorCS", {"start": v(-12.7, -47.78) * mm, "mid": v(-10.11, -47.25) * mm, "end": v(-7.95, -45.73) * mm});
            skArc(sketch, "E235.MirrorCS", {"start": v(-13.93, -28.84) * mm, "mid": v(-21.5, -27.27) * mm, "end": v(-29.18, -26.5) * mm});
            skArc(sketch, "E236.MirrorCS", {"start": v(-24.52, -44.28) * mm, "mid": v(-24.93, -43.04) * mm, "end": v(-25.32, -41.8) * mm});
            skArc(sketch, "E237.MirrorCS", {"start": v(-13.33, -26.56) * mm, "mid": v(-21.4, -24.9) * mm, "end": v(-29.62, -24.13) * mm});
            skPoint(sketch, "E238.MirrorP", {"position": v(-13.33, -26.56) * mm});
            skPoint(sketch, "E239.MirrorP", {"position": v(-27.18, -26.62) * mm});
            skArc(sketch, "E240.MirrorCS", {"start": v(-9.42, -43.73) * mm, "mid": v(-7.48, -37.32) * mm, "end": v(-9.4, -30.9) * mm});
            skPoint(sketch, "E241.MirrorP", {"position": v(-13.93, -28.84) * mm});
            skArc(sketch, "E242.MirrorCS", {"start": v(-29.18, -26.5) * mm, "mid": v(-29.4, -25.31) * mm, "end": v(-29.62, -24.13) * mm});
            skLineSegment(sketch, "E243", {"start": v(-65.43, 0) * mm, "end": v(71.76, 0) * mm, "construction": true});
            skLineSegment(sketch, "E244", {"start": v(0, 78.2) * mm, "end": v(0, -66.26) * mm, "construction": true});
            skPoint(sketch, "E245", {"position": v(0, 0) * mm});
            skSolve(sketch);
        }
        {
            var Q0;
            Q0=qCreatedBy(makeId("Top.planeOp"),FACE);
            var sketch = newSketch(context, id + "F6", { "sketchPlane" : qUnion([Q0])});
            skCircle(sketch, "E246", {"center": v(12.7, 41.27) * mm, "radius": 1.59 * mm});
            skCircle(sketch, "E247", {"center": v(12.7, 33.34) * mm, "radius": 1.59 * mm});
            skCircle(sketch, "E248", {"center": v(22.23, 9.52) * mm, "radius": 1.59 * mm});
            skCircle(sketch, "E249.MirrorC", {"center": v(-12.7, 41.27) * mm, "radius": 1.59 * mm});
            skCircle(sketch, "E250.MirrorC", {"center": v(-12.7, 33.34) * mm, "radius": 1.59 * mm});
            skCircle(sketch, "E251.MirrorC", {"center": v(-22.23, 9.52) * mm, "radius": 1.59 * mm});
            skCircle(sketch, "E252.MirrorC", {"center": v(-22.23, -9.52) * mm, "radius": 1.59 * mm});
            skCircle(sketch, "E253.MirrorC", {"center": v(-12.7, -33.34) * mm, "radius": 1.59 * mm});
            skCircle(sketch, "E254.MirrorC", {"center": v(-12.7, -41.27) * mm, "radius": 1.59 * mm});
            skCircle(sketch, "E255.MirrorC", {"center": v(22.23, -9.52) * mm, "radius": 1.59 * mm});
            skCircle(sketch, "E256.MirrorC", {"center": v(12.7, -41.27) * mm, "radius": 1.59 * mm});
            skCircle(sketch, "E257.MirrorC", {"center": v(12.7, -33.34) * mm, "radius": 1.59 * mm});
            skSolve(sketch);
        }
        {
            var Q0;
            Q0 = qSketchRegion(id + "F6", true);
            extrude(context, id + "F7", {"entities" : qUnion([Q0]), "operationType" : NewBodyOperationType.REMOVE, "endBound" : BoundingType.THROUGH_ALL, "oppositeDirection" : true, "depth" : 25.4 * mm});
        }
        {
            var Q0;
            Q0=makeQuery(id+"F1.opExtrude","CAP_FACE",FACE,{"disambiguationData":[OSD([sQuery(id+"F0.wireOp",EDGE,"E8"),sQuery(id+"F0.wireOp",EDGE,"E11"),sQuery(id+"F0.wireOp",EDGE,"E12.MirrorCS"),sQuery(id+"F0.wireOp",EDGE,"E13.filletArc"),sQuery(id+"F0.wireOp",EDGE,"E14.MirrorCS")])],"isStart":false});
            cPlane(context, id + "F8", {"entities" : qUnion([Q0]), "cplaneType" : CPlaneType.OFFSET, "offset" : 0 * mm, "width" : 152.4 * mm, "height" : 152.4 * mm});
        }
        {
            var Q0;
            Q0=qCreatedBy(makeId("Top.planeOp"),FACE);
            var sketch = newSketch(context, id + "F9", { "sketchPlane" : qUnion([Q0])});
            skArc(sketch, "E258.0", {"start": v(18.64, 46.24) * mm, "mid": v(19.5, 45.8) * mm, "end": v(20.4, 45.4) * mm});
            skArc(sketch, "E258.1", {"start": v(18.64, 46.24) * mm, "mid": v(15.77, 47.4) * mm, "end": v(12.7, 47.78) * mm});
            skArc(sketch, "E258.4", {"start": v(7.95, 45.73) * mm, "mid": v(5.14, 37.83) * mm, "end": v(7.36, 29.74) * mm});
            skArc(sketch, "E258.5", {"start": v(12.7, 47.78) * mm, "mid": v(10.11, 47.25) * mm, "end": v(7.95, 45.73) * mm});
            skArc(sketch, "E259.2", {"start": v(9.4, 30.9) * mm, "mid": v(10.37, 29.9) * mm, "end": v(11.63, 29.31) * mm});
            skArc(sketch, "E260.0", {"start": v(9.42, 43.73) * mm, "mid": v(7.48, 37.32) * mm, "end": v(9.4, 30.9) * mm});
            skArc(sketch, "E260.1", {"start": v(12.52, 45.43) * mm, "mid": v(10.76, 44.96) * mm, "end": v(9.42, 43.73) * mm});
            skArc(sketch, "E260.2", {"start": v(17.5, 44.19) * mm, "mid": v(15.1, 45.14) * mm, "end": v(12.52, 45.43) * mm});
            skArc(sketch, "E260.3", {"start": v(17.5, 44.19) * mm, "mid": v(19.58, 43.19) * mm, "end": v(21.77, 42.45) * mm});
            skPoint(sketch, "E261.visualSharp", {"position": v(9.56, 27.1) * mm});
            skArc(sketch, "E261.filletArc", {"start": v(7.36, 29.74) * mm, "mid": v(9.02, 28) * mm, "end": v(11.21, 27) * mm});
            skArc(sketch, "E262.0", {"start": v(21.77, 42.45) * mm, "mid": v(21.1, 43.93) * mm, "end": v(20.4, 45.4) * mm});
            skArc(sketch, "E263.0", {"start": v(22.37, 1.43) * mm, "mid": v(26.9, 2.03) * mm, "end": v(31.4, 2.9) * mm});
            skArc(sketch, "E263.1", {"start": v(15.91, 14.6) * mm, "mid": v(14.96, 5.96) * mm, "end": v(22.37, 1.43) * mm});
            skArc(sketch, "E264.2", {"start": v(17.82, 13.22) * mm, "mid": v(17.02, 7.1) * mm, "end": v(22.23, 3.78) * mm});
            skArc(sketch, "E264.3", {"start": v(22.23, 3.78) * mm, "mid": v(26.73, 4.38) * mm, "end": v(31.18, 5.25) * mm});
            skArc(sketch, "E265.0", {"start": v(31.18, 5.25) * mm, "mid": v(31.3, 4.07) * mm, "end": v(31.4, 2.9) * mm});
            skArc(sketch, "E266", {"start": v(16.93, 16.78) * mm, "mid": v(16.3, 22.3) * mm, "end": v(12.6, 26.44) * mm});
            skArc(sketch, "E267.filletArc", {"start": v(15.91, 14.6) * mm, "mid": v(16.55, 15.63) * mm, "end": v(16.93, 16.78) * mm});
            skArc(sketch, "E268", {"start": v(19.44, 17.21) * mm, "mid": v(17.94, 24.06) * mm, "end": v(12.84, 28.86) * mm});
            skArc(sketch, "E269", {"start": v(18.26, 13.83) * mm, "mid": v(19.04, 15.46) * mm, "end": v(19.44, 17.21) * mm});
            skPoint(sketch, "E270.visualSharp", {"position": v(12, 29.24) * mm});
            skArc(sketch, "E270.filletArc", {"start": v(12.84, 28.86) * mm, "mid": v(12.25, 29.12) * mm, "end": v(11.63, 29.31) * mm});
            skArc(sketch, "E271.filletArc", {"start": v(17.82, 13.22) * mm, "mid": v(18.05, 13.52) * mm, "end": v(18.26, 13.83) * mm});
            skPoint(sketch, "E272.visualSharp", {"position": v(11.7, 26.9) * mm});
            skArc(sketch, "E272.filletArc", {"start": v(12.6, 26.44) * mm, "mid": v(11.93, 26.77) * mm, "end": v(11.21, 27) * mm});
            skArc(sketch, "E273.MirrorCS", {"start": v(-12.84, 28.86) * mm, "mid": v(-12.25, 29.12) * mm, "end": v(-11.63, 29.31) * mm});
            skArc(sketch, "E274.MirrorCS", {"start": v(-12.6, 26.44) * mm, "mid": v(-11.93, 26.77) * mm, "end": v(-11.21, 27) * mm});
            skArc(sketch, "E275.MirrorCS", {"start": v(-17.82, 13.22) * mm, "mid": v(-18.05, 13.52) * mm, "end": v(-18.26, 13.83) * mm});
            skArc(sketch, "E276.MirrorCS", {"start": v(-18.64, 46.24) * mm, "mid": v(-19.5, 45.8) * mm, "end": v(-20.4, 45.4) * mm});
            skArc(sketch, "E277.MirrorCS", {"start": v(-15.91, 14.6) * mm, "mid": v(-16.55, 15.63) * mm, "end": v(-16.93, 16.78) * mm});
            skArc(sketch, "E278.MirrorCS", {"start": v(-31.18, 5.25) * mm, "mid": v(-31.3, 4.07) * mm, "end": v(-31.4, 2.9) * mm});
            skArc(sketch, "E279.MirrorCS", {"start": v(-9.4, 30.9) * mm, "mid": v(-10.37, 29.9) * mm, "end": v(-11.63, 29.31) * mm});
            skArc(sketch, "E280.MirrorCS", {"start": v(-21.77, 42.45) * mm, "mid": v(-21.1, 43.93) * mm, "end": v(-20.4, 45.4) * mm});
            skArc(sketch, "E281.MirrorCS", {"start": v(-12.52, 45.43) * mm, "mid": v(-10.76, 44.96) * mm, "end": v(-9.42, 43.73) * mm});
            skArc(sketch, "E282.MirrorCS", {"start": v(-9.42, 43.73) * mm, "mid": v(-7.48, 37.32) * mm, "end": v(-9.4, 30.9) * mm});
            skArc(sketch, "E283.MirrorCS", {"start": v(-22.37, 1.43) * mm, "mid": v(-26.9, 2.03) * mm, "end": v(-31.4, 2.9) * mm});
            skArc(sketch, "E284.MirrorCS", {"start": v(-12.7, 47.78) * mm, "mid": v(-10.11, 47.25) * mm, "end": v(-7.95, 45.73) * mm});
            skArc(sketch, "E285.MirrorCS", {"start": v(-18.64, 46.24) * mm, "mid": v(-15.77, 47.4) * mm, "end": v(-12.7, 47.78) * mm});
            skPoint(sketch, "E286.MirrorP", {"position": v(-12, 29.24) * mm});
            skArc(sketch, "E287.MirrorCS", {"start": v(-16.93, 16.78) * mm, "mid": v(-16.3, 22.3) * mm, "end": v(-12.6, 26.44) * mm});
            skArc(sketch, "E288.MirrorCS", {"start": v(-7.36, 29.74) * mm, "mid": v(-9.02, 28) * mm, "end": v(-11.21, 27) * mm});
            skPoint(sketch, "E289.MirrorP", {"position": v(-9.56, 27.1) * mm});
            skPoint(sketch, "E290.MirrorP", {"position": v(-11.7, 26.9) * mm});
            skArc(sketch, "E291.MirrorCS", {"start": v(-18.26, 13.83) * mm, "mid": v(-19.04, 15.46) * mm, "end": v(-19.44, 17.21) * mm});
            skArc(sketch, "E292.MirrorCS", {"start": v(-19.44, 17.21) * mm, "mid": v(-17.94, 24.06) * mm, "end": v(-12.84, 28.86) * mm});
            skArc(sketch, "E293.MirrorCS", {"start": v(-17.5, 44.19) * mm, "mid": v(-15.1, 45.14) * mm, "end": v(-12.52, 45.43) * mm});
            skArc(sketch, "E294.MirrorCS", {"start": v(-17.82, 13.22) * mm, "mid": v(-17.02, 7.1) * mm, "end": v(-22.23, 3.78) * mm});
            skArc(sketch, "E295.MirrorCS", {"start": v(-15.91, 14.6) * mm, "mid": v(-14.96, 5.96) * mm, "end": v(-22.37, 1.43) * mm});
            skArc(sketch, "E296.MirrorCS", {"start": v(-17.5, 44.19) * mm, "mid": v(-19.58, 43.19) * mm, "end": v(-21.77, 42.45) * mm});
            skArc(sketch, "E297.MirrorCS", {"start": v(-7.95, 45.73) * mm, "mid": v(-5.14, 37.83) * mm, "end": v(-7.36, 29.74) * mm});
            skArc(sketch, "E298.MirrorCS", {"start": v(-22.23, 3.78) * mm, "mid": v(-26.73, 4.38) * mm, "end": v(-31.18, 5.25) * mm});
            skArc(sketch, "E299.MirrorCS", {"start": v(12.6, -26.44) * mm, "mid": v(11.93, -26.77) * mm, "end": v(11.21, -27) * mm});
            skArc(sketch, "E300.MirrorCS", {"start": v(12.84, -28.86) * mm, "mid": v(12.25, -29.12) * mm, "end": v(11.63, -29.31) * mm});
            skArc(sketch, "E301.MirrorCS", {"start": v(9.4, -30.9) * mm, "mid": v(10.37, -29.9) * mm, "end": v(11.63, -29.31) * mm});
            skArc(sketch, "E302.MirrorCS", {"start": v(15.91, -14.6) * mm, "mid": v(16.55, -15.63) * mm, "end": v(16.93, -16.78) * mm});
            skArc(sketch, "E303.MirrorCS", {"start": v(17.82, -13.22) * mm, "mid": v(18.05, -13.52) * mm, "end": v(18.26, -13.83) * mm});
            skArc(sketch, "E304.MirrorCS", {"start": v(12.52, -45.43) * mm, "mid": v(10.76, -44.96) * mm, "end": v(9.42, -43.73) * mm});
            skArc(sketch, "E305.MirrorCS", {"start": v(7.36, -29.74) * mm, "mid": v(9.02, -28) * mm, "end": v(11.21, -27) * mm});
            skArc(sketch, "E306.MirrorCS", {"start": v(18.26, -13.83) * mm, "mid": v(19.04, -15.46) * mm, "end": v(19.44, -17.21) * mm});
            skArc(sketch, "E307.MirrorCS", {"start": v(9.42, -43.73) * mm, "mid": v(7.48, -37.32) * mm, "end": v(9.4, -30.9) * mm});
            skArc(sketch, "E308.MirrorCS", {"start": v(15.91, -14.6) * mm, "mid": v(14.96, -5.96) * mm, "end": v(22.37, -1.43) * mm});
            skArc(sketch, "E309.MirrorCS", {"start": v(12.7, -47.78) * mm, "mid": v(10.11, -47.25) * mm, "end": v(7.95, -45.73) * mm});
            skArc(sketch, "E310.MirrorCS", {"start": v(7.95, -45.73) * mm, "mid": v(5.14, -37.83) * mm, "end": v(7.36, -29.74) * mm});
            skArc(sketch, "E311.MirrorCS", {"start": v(18.64, -46.24) * mm, "mid": v(15.77, -47.4) * mm, "end": v(12.7, -47.78) * mm});
            skPoint(sketch, "E312.MirrorP", {"position": v(11.7, -26.9) * mm});
            skArc(sketch, "E313.MirrorCS", {"start": v(19.44, -17.21) * mm, "mid": v(17.94, -24.06) * mm, "end": v(12.84, -28.86) * mm});
            skArc(sketch, "E314.MirrorCS", {"start": v(16.93, -16.78) * mm, "mid": v(16.3, -22.3) * mm, "end": v(12.6, -26.44) * mm});
            skArc(sketch, "E315.MirrorCS", {"start": v(17.82, -13.22) * mm, "mid": v(17.02, -7.1) * mm, "end": v(22.23, -3.78) * mm});
            skPoint(sketch, "E316.MirrorP", {"position": v(12, -29.24) * mm});
            skPoint(sketch, "E317.MirrorP", {"position": v(9.56, -27.1) * mm});
            skArc(sketch, "E318.MirrorCS", {"start": v(17.5, -44.19) * mm, "mid": v(15.1, -45.14) * mm, "end": v(12.52, -45.43) * mm});
            skPoint(sketch, "E319.MirrorCS.end.orphan", {"position": v(31.4, -2.9) * mm});
            skPoint(sketch, "E319.MirrorCS.start.orphan", {"position": v(31.18, -5.25) * mm});
            skArc(sketch, "E320.0", {"start": v(22.48, -1.44) * mm, "mid": v(27.1, -2.06) * mm, "end": v(31.65, -2.95) * mm});
            skArc(sketch, "E321.0", {"start": v(22.24, -3.78) * mm, "mid": v(26.96, -4.42) * mm, "end": v(31.62, -5.35) * mm});
            skArc(sketch, "E322.0", {"start": v(31.65, -2.95) * mm, "mid": v(31.65, -4.15) * mm, "end": v(31.62, -5.35) * mm});
            skPoint(sketch, "E323.MirrorCS.end.orphan", {"position": v(20.4, -45.4) * mm});
            skPoint(sketch, "E323.MirrorCS.start.orphan", {"position": v(21.77, -42.45) * mm});
            skArc(sketch, "E324.0", {"start": v(24.52, -44.28) * mm, "mid": v(24.93, -43.04) * mm, "end": v(25.32, -41.8) * mm});
            skArc(sketch, "E325.0", {"start": v(17.5, -44.19) * mm, "mid": v(20.44, -42.86) * mm, "end": v(23.57, -42.06) * mm});
            skArc(sketch, "E326.0", {"start": v(18.64, -46.24) * mm, "mid": v(21.22, -45.08) * mm, "end": v(23.96, -44.37) * mm});
            skArc(sketch, "E327.0", {"start": v(23.57, -42.06) * mm, "mid": v(24.45, -41.92) * mm, "end": v(25.32, -41.8) * mm});
            skArc(sketch, "E328.0", {"start": v(23.96, -44.37) * mm, "mid": v(24.24, -44.33) * mm, "end": v(24.52, -44.28) * mm});
            skArc(sketch, "E329.MirrorCS", {"start": v(-12.84, -28.86) * mm, "mid": v(-12.25, -29.12) * mm, "end": v(-11.63, -29.31) * mm});
            skArc(sketch, "E330.MirrorCS", {"start": v(-23.96, -44.37) * mm, "mid": v(-24.24, -44.33) * mm, "end": v(-24.52, -44.28) * mm});
            skArc(sketch, "E331.MirrorCS", {"start": v(-31.65, -2.95) * mm, "mid": v(-31.65, -4.15) * mm, "end": v(-31.62, -5.35) * mm});
            skArc(sketch, "E332.MirrorCS", {"start": v(-12.6, -26.44) * mm, "mid": v(-11.93, -26.77) * mm, "end": v(-11.21, -27) * mm});
            skArc(sketch, "E333.MirrorCS", {"start": v(-23.57, -42.06) * mm, "mid": v(-24.45, -41.92) * mm, "end": v(-25.32, -41.8) * mm});
            skArc(sketch, "E334.MirrorCS", {"start": v(-24.52, -44.28) * mm, "mid": v(-24.93, -43.04) * mm, "end": v(-25.32, -41.8) * mm});
            skArc(sketch, "E335.MirrorCS", {"start": v(-17.82, -13.22) * mm, "mid": v(-18.05, -13.52) * mm, "end": v(-18.26, -13.83) * mm});
            skArc(sketch, "E336.MirrorCS", {"start": v(-15.91, -14.6) * mm, "mid": v(-16.55, -15.63) * mm, "end": v(-16.93, -16.78) * mm});
            skPoint(sketch, "E337.MirrorP", {"position": v(-31.18, -5.25) * mm});
            skArc(sketch, "E338.MirrorCS", {"start": v(-17.5, -44.19) * mm, "mid": v(-20.44, -42.86) * mm, "end": v(-23.57, -42.06) * mm});
            skPoint(sketch, "E339.MirrorP", {"position": v(-31.4, -2.9) * mm});
            skPoint(sketch, "E340.MirrorP", {"position": v(-20.4, -45.4) * mm});
            skArc(sketch, "E341.MirrorCS", {"start": v(-18.64, -46.24) * mm, "mid": v(-21.22, -45.08) * mm, "end": v(-23.96, -44.37) * mm});
            skPoint(sketch, "E342.MirrorP", {"position": v(-21.77, -42.45) * mm});
            skArc(sketch, "E343.MirrorCS", {"start": v(-7.36, -29.74) * mm, "mid": v(-9.02, -28) * mm, "end": v(-11.21, -27) * mm});
            skArc(sketch, "E344.MirrorCS", {"start": v(-16.93, -16.78) * mm, "mid": v(-16.3, -22.3) * mm, "end": v(-12.6, -26.44) * mm});
            skPoint(sketch, "E345.MirrorP", {"position": v(-9.56, -27.1) * mm});
            skArc(sketch, "E346.MirrorCS", {"start": v(-19.44, -17.21) * mm, "mid": v(-17.94, -24.06) * mm, "end": v(-12.84, -28.86) * mm});
            skArc(sketch, "E347.MirrorCS", {"start": v(-22.48, -1.44) * mm, "mid": v(-27.1, -2.06) * mm, "end": v(-31.65, -2.95) * mm});
            skArc(sketch, "E348.MirrorCS", {"start": v(-12.52, -45.43) * mm, "mid": v(-10.76, -44.96) * mm, "end": v(-9.42, -43.73) * mm});
            skArc(sketch, "E349.MirrorCS", {"start": v(-22.24, -3.78) * mm, "mid": v(-26.96, -4.42) * mm, "end": v(-31.62, -5.35) * mm});
            skPoint(sketch, "E350.MirrorP", {"position": v(-11.7, -26.9) * mm});
            skArc(sketch, "E351.MirrorCS", {"start": v(-18.26, -13.83) * mm, "mid": v(-19.04, -15.46) * mm, "end": v(-19.44, -17.21) * mm});
            skArc(sketch, "E352.MirrorCS", {"start": v(-15.91, -14.6) * mm, "mid": v(-14.96, -5.96) * mm, "end": v(-22.37, -1.43) * mm});
            skArc(sketch, "E353.MirrorCS", {"start": v(-17.82, -13.22) * mm, "mid": v(-17.02, -7.1) * mm, "end": v(-22.23, -3.78) * mm});
            skArc(sketch, "E354.MirrorCS", {"start": v(-18.64, -46.24) * mm, "mid": v(-15.77, -47.4) * mm, "end": v(-12.7, -47.78) * mm});
            skArc(sketch, "E355.MirrorCS", {"start": v(-9.4, -30.9) * mm, "mid": v(-10.37, -29.9) * mm, "end": v(-11.63, -29.31) * mm});
            skArc(sketch, "E356.MirrorCS", {"start": v(-7.95, -45.73) * mm, "mid": v(-5.14, -37.83) * mm, "end": v(-7.36, -29.74) * mm});
            skArc(sketch, "E357.MirrorCS", {"start": v(-9.42, -43.73) * mm, "mid": v(-7.48, -37.32) * mm, "end": v(-9.4, -30.9) * mm});
            skArc(sketch, "E358.MirrorCS", {"start": v(-12.7, -47.78) * mm, "mid": v(-10.11, -47.25) * mm, "end": v(-7.95, -45.73) * mm});
            skPoint(sketch, "E359.MirrorP", {"position": v(-12, -29.24) * mm});
            skArc(sketch, "E360.MirrorCS", {"start": v(-17.5, -44.19) * mm, "mid": v(-15.1, -45.14) * mm, "end": v(-12.52, -45.43) * mm});
            skArc(sketch, "E361", {"start": v(22.48, -1.44) * mm, "mid": v(22.43, -1.43) * mm, "end": v(22.37, -1.43) * mm});
            skArc(sketch, "E362", {"start": v(22.24, -3.78) * mm, "mid": v(22.24, -3.78) * mm, "end": v(22.23, -3.78) * mm});
            skArc(sketch, "E363.MirrorCS", {"start": v(-22.48, -1.44) * mm, "mid": v(-22.43, -1.43) * mm, "end": v(-22.37, -1.43) * mm});
            skArc(sketch, "E364.MirrorCS", {"start": v(-22.24, -3.78) * mm, "mid": v(-22.24, -3.78) * mm, "end": v(-22.23, -3.78) * mm});
            skSolve(sketch);
        }
        {
            var Q0;
            Q0 = qSketchRegion(id + "F9", true);
            extrude(context, id + "F10", {"entities" : qUnion([Q0]), "operationType" : NewBodyOperationType.ADD, "depth" : 6.35 * mm});
        }
        {
            var Q0;
            Q0=qCreatedBy(makeId("Top.planeOp"),FACE);
            var sketch = newSketch(context, id + "F11", { "sketchPlane" : qUnion([Q0])});
            skLineSegment(sketch, "E365", {"start": v(91.05, 0) * mm, "end": v(-86.67, 0) * mm, "construction": true});
            skLineSegment(sketch, "E366", {"start": v(0, 79.99) * mm, "end": v(0, -101.6) * mm, "construction": true});
            skPoint(sketch, "E367", {"position": v(0, 0) * mm});
            skPoint(sketch, "E368", {"position": v(-22.23, 0) * mm});
            skPoint(sketch, "E369", {"position": v(22.23, 0) * mm});
            skPoint(sketch, "E370", {"position": v(0, 44.45) * mm});
            skPoint(sketch, "E371", {"position": v(-11.43, 76.2) * mm});
            skPoint(sketch, "E372", {"position": v(11.43, 76.2) * mm});
            skPoint(sketch, "E373", {"position": v(-6.35, 50.8) * mm});
            skPoint(sketch, "E374", {"position": v(6.35, 50.8) * mm});
            skLineSegment(sketch, "E375", {"start": v(-6.35, 44.45) * mm, "end": v(6.35, 44.45) * mm, "construction": true});
            skArc(sketch, "E376", {"start": v(-1.54, 44.64) * mm, "mid": v(0, 44.45) * mm, "end": v(1.54, 44.64) * mm});
            skLineSegment(sketch, "E377", {"start": v(-6.35, 44.45) * mm, "end": v(0, 50.8) * mm, "construction": true});
            skLineSegment(sketch, "E378", {"start": v(0, 50.8) * mm, "end": v(6.35, 44.45) * mm, "construction": true});
            skPoint(sketch, "E379", {"position": v(-4.5, 46.3) * mm});
            skPoint(sketch, "E380", {"position": v(4.5, 46.3) * mm});
            skArc(sketch, "E381", {"start": v(-11.43, 76.2) * mm, "mid": v(-9.27, 61.75) * mm, "end": v(-5.06, 47.76) * mm});
            skArc(sketch, "E382", {"start": v(5.06, 47.76) * mm, "mid": v(9.27, 61.75) * mm, "end": v(11.43, 76.2) * mm});
            skArc(sketch, "E383.filletArc", {"start": v(-5.06, 47.76) * mm, "mid": v(-3.68, 45.77) * mm, "end": v(-1.54, 44.64) * mm});
            skArc(sketch, "E384.filletArc", {"start": v(1.54, 44.64) * mm, "mid": v(3.68, 45.77) * mm, "end": v(5.06, 47.76) * mm});
            skLineSegment(sketch, "E385", {"start": v(19.05, -57.15) * mm, "end": v(-20.16, -57.15) * mm, "construction": true});
            skLineSegment(sketch, "E386", {"start": v(16.51, -19.05) * mm, "end": v(-17.62, -19.05) * mm, "construction": true});
            skArc(sketch, "E387", {"start": v(-11.43, 76.2) * mm, "mid": v(-20.39, 28.96) * mm, "end": v(-17.62, -19.05) * mm});
            skArc(sketch, "E388", {"start": v(16.51, -19.05) * mm, "mid": v(19.83, 28.89) * mm, "end": v(11.43, 76.2) * mm});
            skArc(sketch, "E389", {"start": v(-19.1, -50.97) * mm, "mid": v(-17.52, -35.05) * mm, "end": v(-17.62, -19.05) * mm});
            skArc(sketch, "E390", {"start": v(16.51, -19.05) * mm, "mid": v(16.39, -34.66) * mm, "end": v(17.86, -50.2) * mm});
            skLineSegment(sketch, "E391", {"start": v(0, -101.6) * mm, "end": v(27.94, -101.6) * mm, "construction": true});
            skLineSegment(sketch, "E392", {"start": v(0, -101.6) * mm, "end": v(-27.94, -101.6) * mm, "construction": true});
            skArc(sketch, "E393", {"start": v(-21.7, -61.04) * mm, "mid": v(-26.64, -79.48) * mm, "end": v(-28.05, -98.52) * mm});
            skArc(sketch, "E394", {"start": v(27.98, -98.33) * mm, "mid": v(26.14, -79.57) * mm, "end": v(20.88, -61.48) * mm});
            skPoint(sketch, "E395", {"position": v(0, -60.96) * mm});
            skArc(sketch, "E396", {"start": v(0, -60.96) * mm, "mid": v(-15.6, -78.3) * mm, "end": v(-26.83, -98.75) * mm});
            skArc(sketch, "E397", {"start": v(26.76, -98.57) * mm, "mid": v(15.54, -78.23) * mm, "end": v(0, -60.96) * mm});
            skPoint(sketch, "E398.visualSharp", {"position": v(-20.16, -57.15) * mm});
            skArc(sketch, "E398.filletArc", {"start": v(-21.7, -61.04) * mm, "mid": v(-20.14, -56.07) * mm, "end": v(-19.1, -50.97) * mm});
            skPoint(sketch, "E399.visualSharp", {"position": v(19.05, -57.15) * mm});
            skArc(sketch, "E399.filletArc", {"start": v(17.86, -50.2) * mm, "mid": v(19.05, -55.93) * mm, "end": v(20.88, -61.48) * mm});
            skPoint(sketch, "E400.visualSharp", {"position": v(-27.94, -101.6) * mm});
            skArc(sketch, "E400.filletArc", {"start": v(-28.05, -98.52) * mm, "mid": v(-27.53, -99.13) * mm, "end": v(-26.83, -98.75) * mm});
            skPoint(sketch, "E401.visualSharp", {"position": v(27.94, -101.6) * mm});
            skArc(sketch, "E401.filletArc", {"start": v(26.76, -98.57) * mm, "mid": v(27.47, -98.95) * mm, "end": v(27.98, -98.33) * mm});
            skPoint(sketch, "E402", {"position": v(15.24, 0) * mm});
            skCircle(sketch, "E403", {"center": v(15.24, 0) * mm, "radius": 1.59 * mm});
            skCircle(sketch, "E404", {"center": v(15.24, 0) * mm, "radius": 3.18 * mm, "construction": true});
            skPoint(sketch, "E405.MirrorP", {"position": v(-15.24, 0) * mm});
            skCircle(sketch, "E406.MirrorC", {"center": v(-15.24, 0) * mm, "radius": 1.59 * mm});
            skCircle(sketch, "E407.MirrorC", {"center": v(-15.24, 0) * mm, "radius": 3.18 * mm, "construction": true});
            skCircle(sketch, "E408.MirrorC", {"center": v(-11.43, 51.44) * mm, "radius": 1.59 * mm});
            skCircle(sketch, "E409.MirrorC", {"center": v(-11.43, 51.44) * mm, "radius": 3.18 * mm, "construction": true});
            skCircle(sketch, "E410.MirrorC", {"center": v(11.43, 51.44) * mm, "radius": 3.18 * mm, "construction": true});
            skCircle(sketch, "E411.MirrorC", {"center": v(11.43, 51.44) * mm, "radius": 1.59 * mm});
            skCircle(sketch, "E412.MirrorC", {"center": v(-11.43, -62.23) * mm, "radius": 1.59 * mm});
            skCircle(sketch, "E413.MirrorC", {"center": v(-11.43, -62.23) * mm, "radius": 3.18 * mm, "construction": true});
            skCircle(sketch, "E414.MirrorC", {"center": v(11.43, -62.23) * mm, "radius": 3.18 * mm, "construction": true});
            skCircle(sketch, "E415.MirrorC", {"center": v(11.43, -62.23) * mm, "radius": 1.59 * mm});
            skSolve(sketch);
        }
        {
            var Q0;
            Q0=makeQuery(id+"F11.imprint","IMPRINT",FACE,{"disambiguationData":[TD([[makeQuery(id+"F11.imprint","IMPRINT",EDGE,{"derivedFrom":sQuery(id+"F11.wireOp",EDGE,"E412.MirrorC")}),-1.0]])]});
            var Q1;
            Q1=makeQuery(id+"F11.imprint","IMPRINT",FACE,{"disambiguationData":[TD([[makeQuery(id+"F11.imprint","IMPRINT",EDGE,{"derivedFrom":sQuery(id+"F11.wireOp",EDGE,"E411.MirrorC")}),1.0]])]});
            var Q2;
            Q2=makeQuery(id+"F11.imprint","IMPRINT",FACE,{"disambiguationData":[TD([[makeQuery(id+"F11.imprint","IMPRINT",EDGE,{"derivedFrom":sQuery(id+"F11.wireOp",EDGE,"E408.MirrorC")}),-1.0]])]});
            var Q3;
            Q3=makeQuery(id+"F11.imprint","IMPRINT",FACE,{"disambiguationData":[TD([[makeQuery(id+"F11.imprint","IMPRINT",EDGE,{"derivedFrom":sQuery(id+"F11.wireOp",EDGE,"E406.MirrorC")}),-1.0]])]});
            var Q4;
            Q4=makeQuery(id+"F11.imprint","IMPRINT",FACE,{"disambiguationData":[TD([[makeQuery(id+"F11.imprint","IMPRINT",EDGE,{"derivedFrom":sQuery(id+"F11.wireOp",EDGE,"E403")}),1.0]])]});
            var Q5;
            Q5=makeQuery(id+"F11.imprint","IMPRINT",FACE,{"disambiguationData":[TD([[makeQuery(id+"F11.imprint","IMPRINT",EDGE,{"derivedFrom":sQuery(id+"F11.wireOp",EDGE,"E415.MirrorC")}),1.0]])]});
            extrude(context, id + "F12", {"entities" : qUnion([Q0, Q1, Q2, Q3, Q4, Q5]), "operationType" : NewBodyOperationType.REMOVE, "oppositeDirection" : true, "depth" : 25.4 * mm});
        }
        {
            var Q0;
            Q0=makeQuery(id+"F10.opExtrude","CAP_EDGE",EDGE,{"disambiguationData":[OSD([sQuery(id+"F9.wireOp",EDGE,"E291.MirrorCS")])],"isStart":false});
            var Q1;
            Q1=makeQuery(id+"F10.opExtrude","CAP_EDGE",EDGE,{"disambiguationData":[OSD([sQuery(id+"F9.wireOp",EDGE,"E292.MirrorCS")])],"isStart":false});
            var Q2;
            Q2=makeQuery(id+"F10.opExtrude","CAP_EDGE",EDGE,{"disambiguationData":[OSD([sQuery(id+"F9.wireOp",EDGE,"E294.MirrorCS")])],"isStart":false});
            var Q3;
            Q3=makeQuery(id+"F10.opExtrude","CAP_EDGE",EDGE,{"disambiguationData":[OSD([sQuery(id+"F9.wireOp",EDGE,"E275.MirrorCS")])],"isStart":false});
            var Q4;
            Q4=makeQuery(id+"F10.opExtrude","CAP_EDGE",EDGE,{"disambiguationData":[OSD([sQuery(id+"F9.wireOp",EDGE,"E298.MirrorCS")])],"isStart":false});
            var Q5;
            Q5=makeQuery(id+"F10.opExtrude","CAP_EDGE",EDGE,{"disambiguationData":[OSD([sQuery(id+"F9.wireOp",EDGE,"E278.MirrorCS")])],"isStart":false});
            var Q6;
            Q6=makeQuery(id+"F10.opExtrude","CAP_EDGE",EDGE,{"disambiguationData":[OSD([sQuery(id+"F9.wireOp",EDGE,"E283.MirrorCS")])],"isStart":false});
            var Q7;
            Q7=makeQuery(id+"F10.opExtrude","CAP_EDGE",EDGE,{"disambiguationData":[OSD([sQuery(id+"F9.wireOp",EDGE,"E295.MirrorCS")])],"isStart":false});
            var Q8;
            Q8=makeQuery(id+"F10.opExtrude","CAP_EDGE",EDGE,{"disambiguationData":[OSD([sQuery(id+"F9.wireOp",EDGE,"E277.MirrorCS")])],"isStart":false});
            var Q9;
            Q9=makeQuery(id+"F10.opExtrude","CAP_EDGE",EDGE,{"disambiguationData":[OSD([sQuery(id+"F9.wireOp",EDGE,"E287.MirrorCS")])],"isStart":false});
            var Q10;
            Q10=makeQuery(id+"F10.opExtrude","CAP_EDGE",EDGE,{"disambiguationData":[OSD([sQuery(id+"F9.wireOp",EDGE,"E284.MirrorCS")])],"isStart":false});
            var Q11;
            Q11=makeQuery(id+"F10.opExtrude","CAP_EDGE",EDGE,{"disambiguationData":[OSD([sQuery(id+"F9.wireOp",EDGE,"E285.MirrorCS")])],"isStart":false});
            var Q12;
            Q12=makeQuery(id+"F10.opExtrude","CAP_EDGE",EDGE,{"disambiguationData":[OSD([sQuery(id+"F9.wireOp",EDGE,"E280.MirrorCS")])],"isStart":false});
            var Q13;
            Q13=makeQuery(id+"F10.opExtrude","CAP_EDGE",EDGE,{"disambiguationData":[OSD([sQuery(id+"F9.wireOp",EDGE,"E276.MirrorCS")])],"isStart":false});
            fillet(context, id + "F13", {"entities" : qUnion([Q0, Q1, Q2, Q3, Q4, Q5, Q6, Q7, Q8, Q9, Q10, Q11, Q12, Q13]), "radius" : 0.92 * mm, "tangentPropagation" : true, "allowEdgeOverflow" : false});
        }
        {
            var Q0;
            Q0=makeQuery(id+"F10.opExtrude","SWEPT_EDGE",EDGE,{"disambiguationData":[OSD([sQuery(id+"F9.wireOp",EDGE,"E280.MirrorCS"),sQuery(id+"F9.wireOp",EDGE,"E296.MirrorCS")])]});
            fillet(context, id + "F14", {"entities" : qUnion([Q0]), "radius" : 0.64 * mm, "tangentPropagation" : true, "allowEdgeOverflow" : false});
        }
    });
